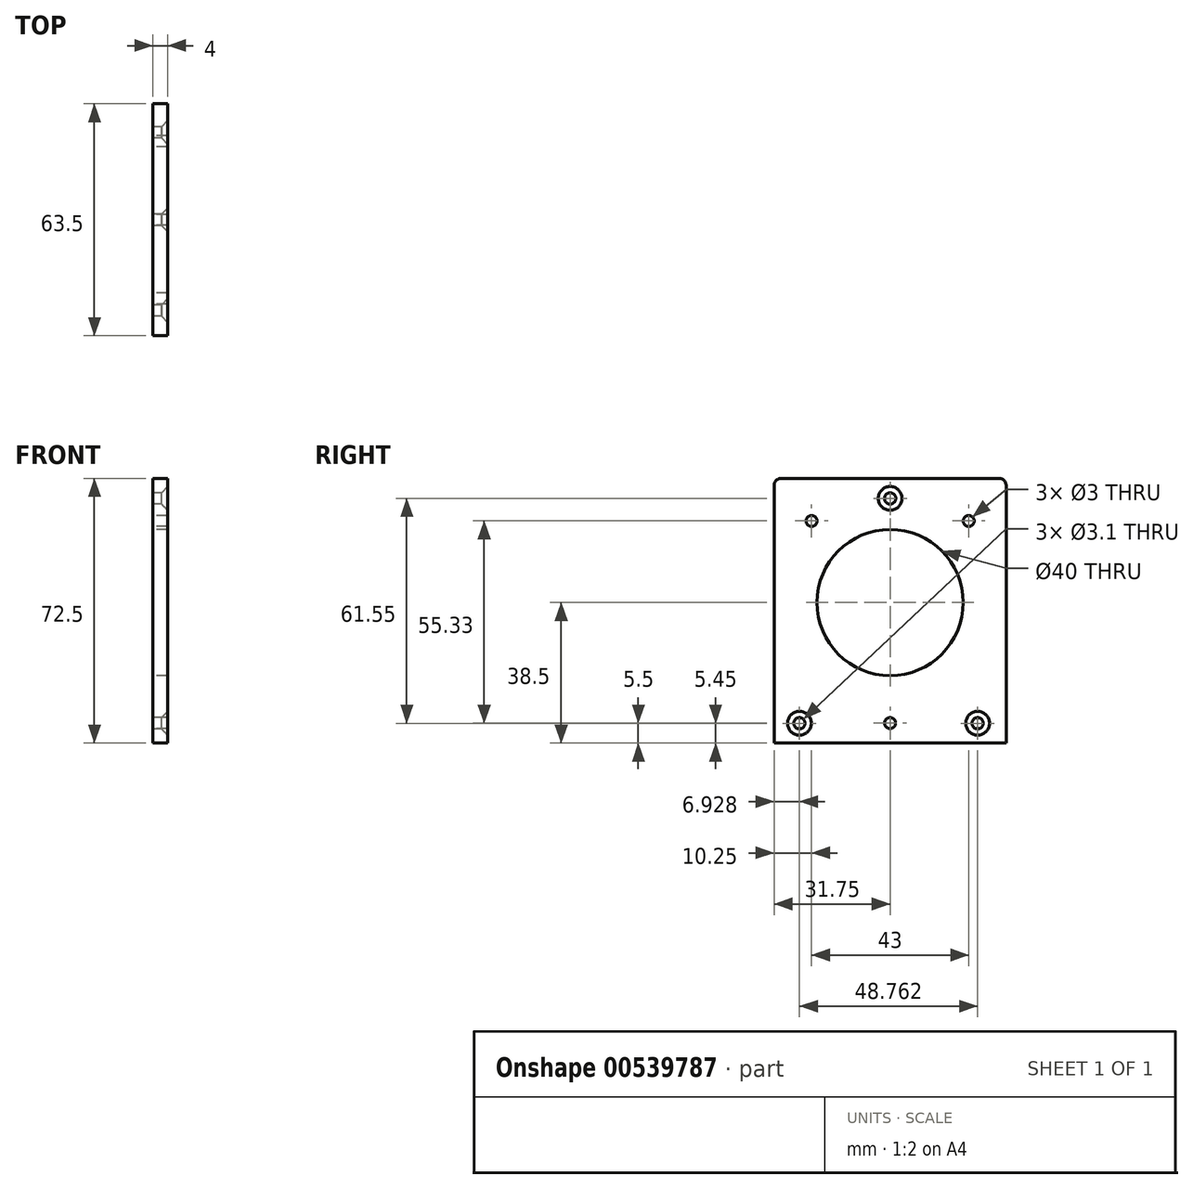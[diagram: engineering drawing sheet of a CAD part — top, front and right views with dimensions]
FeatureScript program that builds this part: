
annotation { "Feature Type Name" : "Feature", "Feature Type Description" : "" }
export const myFeature = defineFeature(function(context is Context, id is Id, definition is map)
    precondition{}
    {
        {
            var Q0;
            Q0=qCreatedBy(makeId("Right.planeOp"),FACE);
            var sketch = newSketch(context, id + "F0", { "sketchPlane" : qUnion([Q0])});
            skLineSegment(sketch, "E0.bottom", {"start": v(29.75, 36.25) * mm, "end": v(-29.75, 36.25) * mm});
            skLineSegment(sketch, "E0.top", {"start": v(31.75, -36.25) * mm, "end": v(-31.75, -36.25) * mm});
            skLineSegment(sketch, "E0.left", {"start": v(31.75, 34.25) * mm, "end": v(31.75, -36.25) * mm});
            skLineSegment(sketch, "E0.right", {"start": v(-31.75, 34.25) * mm, "end": v(-31.75, -36.25) * mm});
            skPoint(sketch, "E0.middle", {"position": v(0, 0) * mm});
            skPoint(sketch, "E1.visualSharp", {"position": v(-31.75, 36.25) * mm});
            skArc(sketch, "E1.filletArc", {"start": v(-29.75, 36.25) * mm, "mid": v(-31.16, 35.66) * mm, "end": v(-31.75, 34.25) * mm});
            skPoint(sketch, "E2.visualSharp", {"position": v(31.75, 36.25) * mm});
            skArc(sketch, "E2.filletArc", {"start": v(31.75, 34.25) * mm, "mid": v(31.16, 35.66) * mm, "end": v(29.75, 36.25) * mm});
            skCircle(sketch, "E3", {"center": v(0, 2.25) * mm, "radius": 20 * mm});
            skCircle(sketch, "E4", {"center": v(-21.5, 24.58) * mm, "radius": 1.5 * mm});
            skCircle(sketch, "E5", {"center": v(21.5, 24.58) * mm, "radius": 1.5 * mm});
            skCircle(sketch, "E6", {"center": v(0, -30.75) * mm, "radius": 1.5 * mm});
            skCircle(sketch, "E7", {"center": v(-24.82, -30.8) * mm, "radius": 1.55 * mm});
            skCircle(sketch, "E8", {"center": v(23.94, -30.8) * mm, "radius": 1.55 * mm});
            skCircle(sketch, "E9", {"center": v(0, 30.75) * mm, "radius": 1.55 * mm});
            skSolve(sketch);
        }
        {
            var Q0;
            Q0 = qSketchRegion(id + "F0", true);
            extrude(context, id + "F1", {"entities" : qUnion([Q0]), "depth" : 4 * mm, "offsetDistance" : 25 * mm});
        }
        {
            var Q0;
            Q0=makeQuery(id+"F1.opExtrude","CAP_EDGE",EDGE,{"disambiguationData":[OSD([sQuery(id+"F0.wireOp",EDGE,"E7")])],"isStart":false});
            var Q1;
            Q1=makeQuery(id+"F1.opExtrude","CAP_EDGE",EDGE,{"disambiguationData":[OSD([sQuery(id+"F0.wireOp",EDGE,"E8")])],"isStart":false});
            var Q2;
            Q2=makeQuery(id+"F1.opExtrude","CAP_EDGE",EDGE,{"disambiguationData":[OSD([sQuery(id+"F0.wireOp",EDGE,"E9")])],"isStart":false});
            chamfer(context, id + "F2", {"entities" : qUnion([Q0, Q1, Q2]), "width" : 1.7 * mm, "tangentPropagation" : true});
        }
    });
